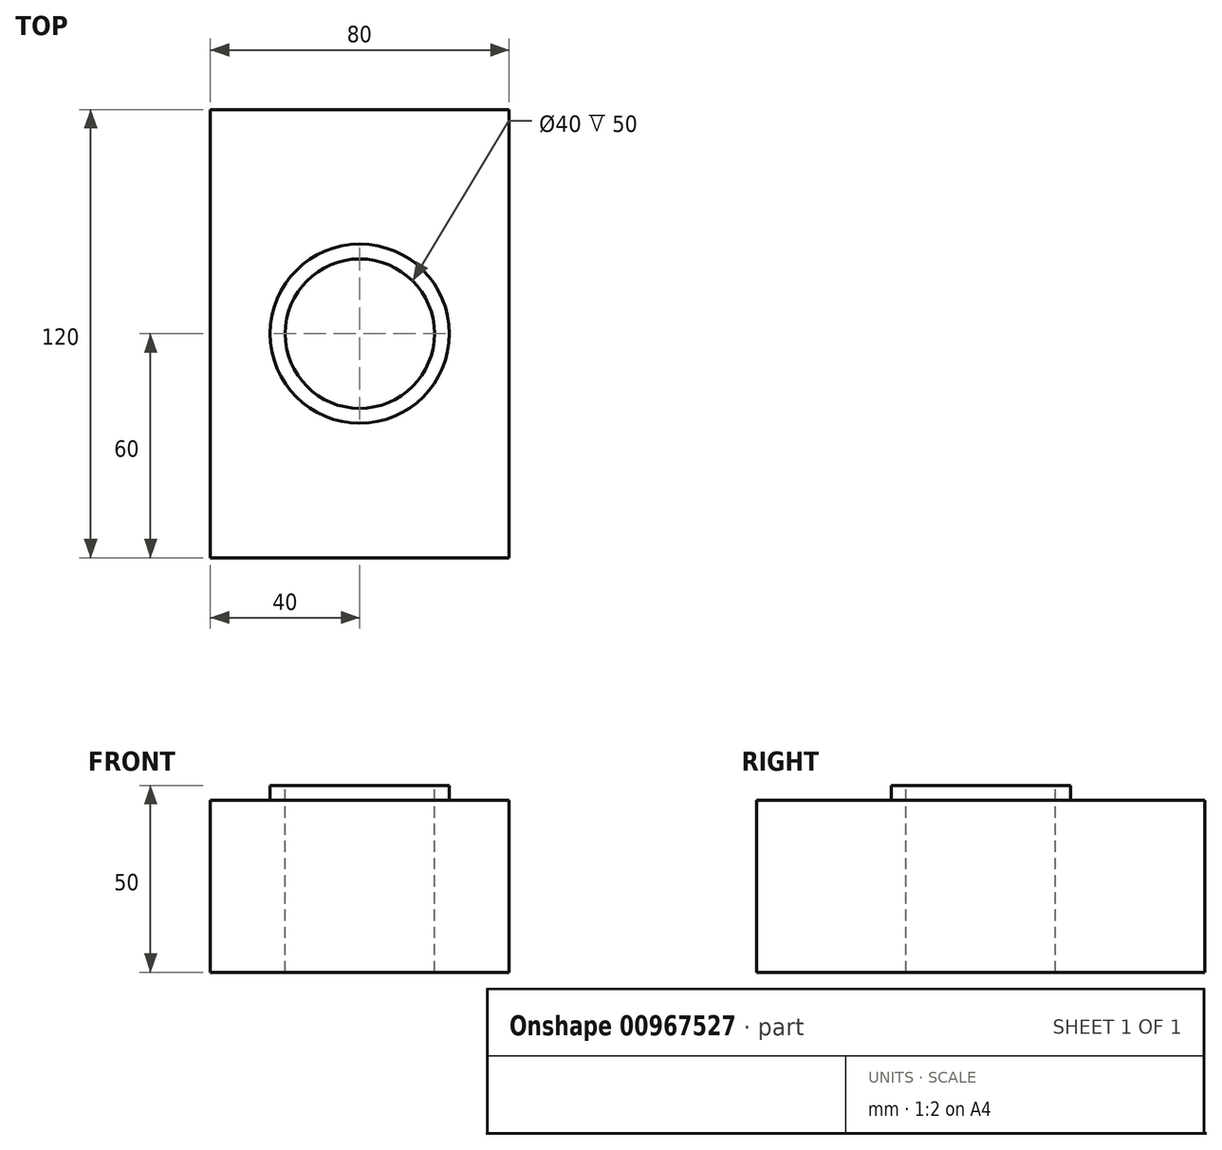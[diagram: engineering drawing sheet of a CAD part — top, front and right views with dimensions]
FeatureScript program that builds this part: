
annotation { "Feature Type Name" : "Feature", "Feature Type Description" : "" }
export const myFeature = defineFeature(function(context is Context, id is Id, definition is map)
    precondition{}
    {
        {
            var Q0;
            Q0=qCreatedBy(makeId("Top.planeOp"),FACE);
            var sketch = newSketch(context, id + "F0", { "sketchPlane" : qUnion([Q0])});
            skLineSegment(sketch, "E0.bottom", {"start": v(-40, 60) * mm, "end": v(40, 60) * mm});
            skLineSegment(sketch, "E0.top", {"start": v(-40, -60) * mm, "end": v(40, -60) * mm});
            skLineSegment(sketch, "E0.left", {"start": v(-40, 60) * mm, "end": v(-40, -60) * mm});
            skLineSegment(sketch, "E0.right", {"start": v(40, 60) * mm, "end": v(40, -60) * mm});
            skSolve(sketch);
        }
        {
            var Q0;
            Q0 = qSketchRegion(id + "F0", true);
            var Q1;
            Q1=makeQuery(id+"F0.imprint","IMPRINT",FACE,{"disambiguationData":[TD([[makeQuery(id+"F0.imprint","IMPRINT",EDGE,{"derivedFrom":sQuery(id+"F0.wireOp",EDGE,"E0.bottom")}),-1.0]])]});
            extrude(context, id + "F1", {"entities" : qUnion([Q0, Q1]), "depth" : 46 * mm, "offsetDistance" : 25 * mm});
        }
        {
            var Q0;
            Q0=makeQuery(id+"F1.opExtrude","CAP_FACE",FACE,{"disambiguationData":[OSD([sQuery(id+"F0.wireOp",EDGE,"E0.bottom"),sQuery(id+"F0.wireOp",EDGE,"E0.top"),sQuery(id+"F0.wireOp",EDGE,"E0.left"),sQuery(id+"F0.wireOp",EDGE,"E0.right")])],"isStart":false});
            var sketch = newSketch(context, id + "F2", { "sketchPlane" : qUnion([Q0])});
            skCircle(sketch, "E1", {"center": v(0, 0) * mm, "radius": 24 * mm});
            skCircle(sketch, "E2", {"center": v(0, 0) * mm, "radius": 20 * mm});
            skSolve(sketch);
        }
        {
            var Q0;
            Q0=makeQuery(id+"F2.imprint","IMPRINT",FACE,{"disambiguationData":[TD([[makeQuery(id+"F2.imprint","IMPRINT",EDGE,{"derivedFrom":sQuery(id+"F2.wireOp",EDGE,"E2")}),1.0]])]});
            extrude(context, id + "F3", {"entities" : qUnion([Q0]), "operationType" : NewBodyOperationType.REMOVE, "oppositeDirection" : true, "depth" : 65 * mm, "offsetDistance" : 25 * mm});
        }
        {
            var Q0;
            Q0=makeQuery(id+"F2.imprint","IMPRINT",FACE,{"disambiguationData":[TD([[makeQuery(id+"F2.imprint","IMPRINT",EDGE,{"derivedFrom":sQuery(id+"F2.wireOp",EDGE,"E1")}),1.0]])]});
            extrude(context, id + "F4", {"entities" : qUnion([Q0]), "operationType" : NewBodyOperationType.ADD, "depth" : 4 * mm, "offsetDistance" : 25 * mm});
        }
    });
